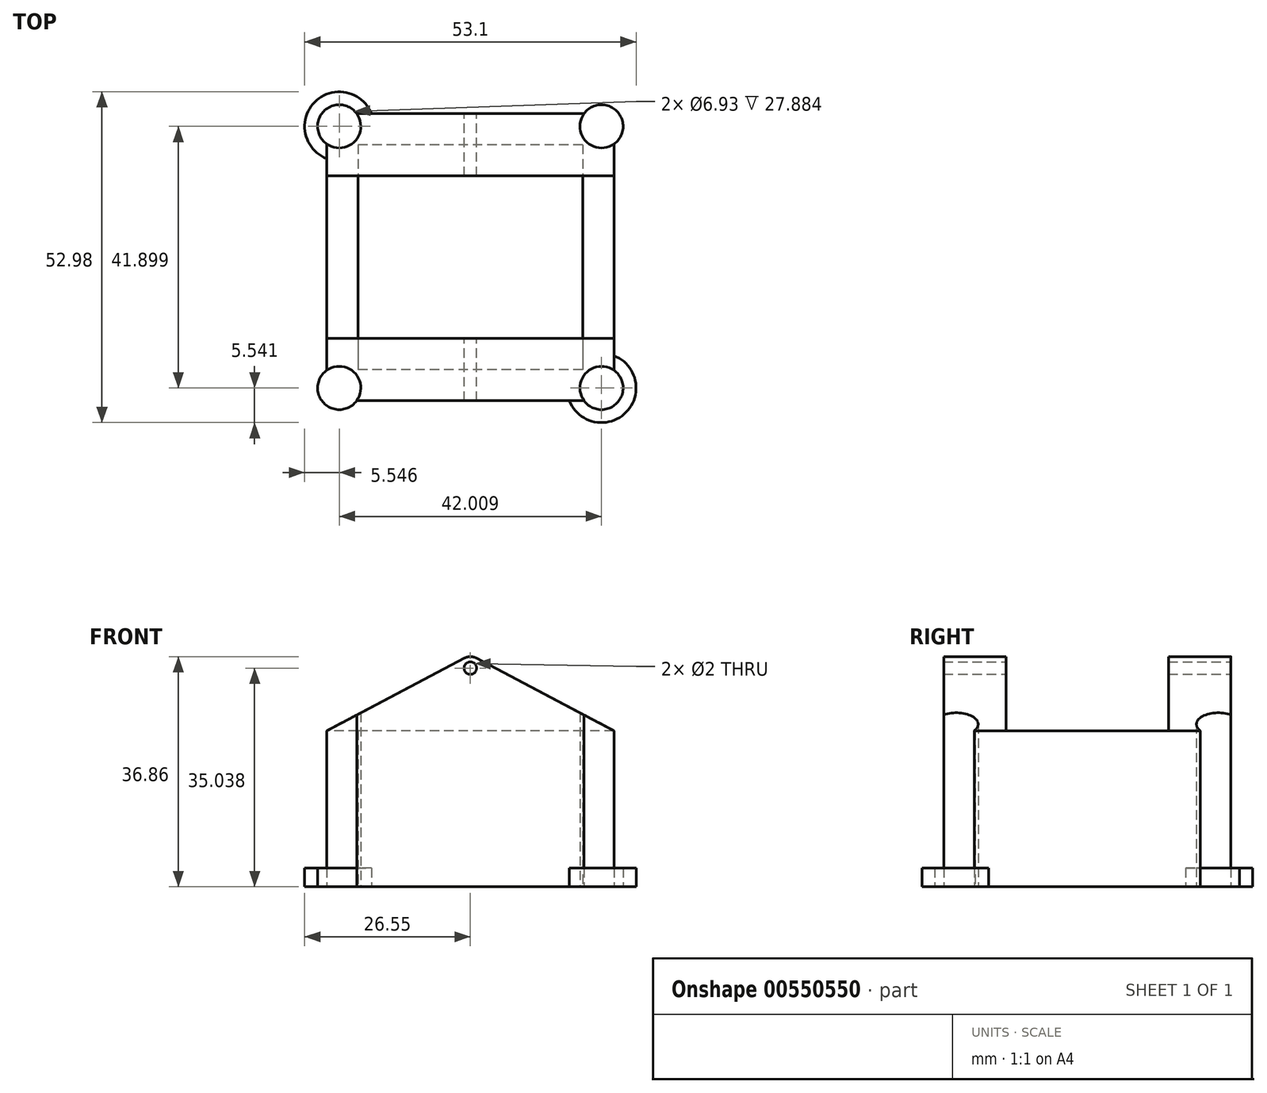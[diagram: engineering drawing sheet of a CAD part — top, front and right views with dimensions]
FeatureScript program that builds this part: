
annotation { "Feature Type Name" : "Feature", "Feature Type Description" : "" }
export const myFeature = defineFeature(function(context is Context, id is Id, definition is map)
    precondition{}
    {
        {
            var Q0;
            Q0=qCreatedBy(makeId("Top.planeOp"),FACE);
            var sketch = newSketch(context, id + "F0", { "sketchPlane" : qUnion([Q0])});
            skLineSegment(sketch, "E0.top", {"start": v(0, 23) * mm, "end": v(-23, 23) * mm});
            skLineSegment(sketch, "E0.right", {"start": v(-23, 0) * mm, "end": v(-23, 23) * mm});
            skCircle(sketch, "E1", {"center": v(-20.22, 20.22) * mm, "radius": 1.65 * mm});
            skCircle(sketch, "E2.MirrorC", {"center": v(20.22, 20.22) * mm, "radius": 1.65 * mm});
            skLineSegment(sketch, "E3.MirrorCS", {"start": v(23, 0) * mm, "end": v(23, 23) * mm});
            skLineSegment(sketch, "E4.MirrorCS", {"start": v(0, 23) * mm, "end": v(23, 23) * mm});
            skLineSegment(sketch, "E5.MirrorCS", {"start": v(0, -23) * mm, "end": v(-23, -23) * mm});
            skCircle(sketch, "E6.MirrorC", {"center": v(-20.22, -20.22) * mm, "radius": 1.65 * mm});
            skLineSegment(sketch, "E7.MirrorCS", {"start": v(-23, 0) * mm, "end": v(-23, -23) * mm});
            skLineSegment(sketch, "E8.MirrorCS", {"start": v(23, 0) * mm, "end": v(23, -23) * mm});
            skCircle(sketch, "E9.MirrorC", {"center": v(20.22, -20.22) * mm, "radius": 1.65 * mm});
            skLineSegment(sketch, "E10.MirrorCS", {"start": v(0, -23) * mm, "end": v(23, -23) * mm});
            skSolve(sketch);
        }
        {
            var Q0;
            Q0 = qSketchRegion(id + "F0", true);
            extrude(context, id + "F1", {"entities" : qUnion([Q0]), "depth" : 25 * mm, "offsetDistance" : 25 * mm});
        }
        {
            var Q0;
            Q0=makeQuery(id+"F1.opExtrude","CAP_FACE",FACE,{"disambiguationData":[OSD([sQuery(id+"F0.wireOp",EDGE,"E0.top"),sQuery(id+"F0.wireOp",EDGE,"E0.right"),sQuery(id+"F0.wireOp",EDGE,"E1"),sQuery(id+"F0.wireOp",EDGE,"E2.MirrorC"),sQuery(id+"F0.wireOp",EDGE,"E3.MirrorCS"),sQuery(id+"F0.wireOp",EDGE,"E4.MirrorCS"),sQuery(id+"F0.wireOp",EDGE,"E5.MirrorCS"),sQuery(id+"F0.wireOp",EDGE,"E6.MirrorC"),sQuery(id+"F0.wireOp",EDGE,"E7.MirrorCS"),sQuery(id+"F0.wireOp",EDGE,"E8.MirrorCS"),sQuery(id+"F0.wireOp",EDGE,"E9.MirrorC"),sQuery(id+"F0.wireOp",EDGE,"E10.MirrorCS")])],"isStart":true});
            var sketch = newSketch(context, id + "F2", { "sketchPlane" : qUnion([Q0])});
            skLineSegment(sketch, "E11.bottom", {"start": v(18, -18) * mm, "end": v(-18, -18) * mm});
            skLineSegment(sketch, "E11.top", {"start": v(18, 18) * mm, "end": v(-18, 18) * mm});
            skLineSegment(sketch, "E11.left", {"start": v(18, -18) * mm, "end": v(18, 18) * mm});
            skLineSegment(sketch, "E11.right", {"start": v(-18, -18) * mm, "end": v(-18, 18) * mm});
            skPoint(sketch, "E11.middle", {"position": v(0, 0) * mm});
            skSolve(sketch);
        }
        {
            var Q0;
            Q0=qCreatedBy(makeId("Front.planeOp"),FACE);
            var sketch = newSketch(context, id + "F3", { "sketchPlane" : qUnion([Q0])});
            skLineSegment(sketch, "E12", {"start": v(0, 25) * mm, "end": v(23, 25) * mm});
            skLineSegment(sketch, "E13", {"start": v(23, 25) * mm, "end": v(0, 37.12) * mm});
            skArc(sketch, "E14", {"start": v(0, 34.04) * mm, "mid": v(1, 35.04) * mm, "end": v(0, 36.04) * mm});
            skArc(sketch, "E15.MirrorCS", {"start": v(0, 34.04) * mm, "mid": v(-1, 35.04) * mm, "end": v(0, 36.04) * mm});
            skLineSegment(sketch, "E16.MirrorCS", {"start": v(-23, 25) * mm, "end": v(0, 37.12) * mm});
            skLineSegment(sketch, "E17.MirrorCS", {"start": v(0, 25) * mm, "end": v(-23, 25) * mm});
            skSolve(sketch);
        }
        {
            var Q0;
            Q0=makeQuery(id+"F3.imprint","IMPRINT",FACE,{"disambiguationData":[TD([[makeQuery(id+"F3.imprint","IMPRINT",EDGE,{"derivedFrom":sQuery(id+"F3.wireOp",EDGE,"E12")}),1.0]])]});
            extrude(context, id + "F4", {"entities" : qUnion([Q0]), "operationType" : NewBodyOperationType.ADD, "endBound" : BoundingType.SYMMETRIC, "depth" : 46 * mm, "offsetDistance" : 25 * mm});
        }
        {
            var Q0;
            Q0=qCreatedBy(makeId("Top.planeOp"),FACE);
            var sketch = newSketch(context, id + "F5", { "sketchPlane" : qUnion([Q0])});
            skCircle(sketch, "E18", {"center": v(-21, 20.95) * mm, "radius": 3.47 * mm});
            skCircle(sketch, "E19.MirrorC", {"center": v(21, 20.95) * mm, "radius": 3.47 * mm});
            skCircle(sketch, "E20.MirrorC", {"center": v(21, -20.95) * mm, "radius": 3.47 * mm});
            skCircle(sketch, "E21.MirrorC", {"center": v(-21, -20.95) * mm, "radius": 3.47 * mm});
            skSolve(sketch);
        }
        {
            var Q0;
            Q0=qCreatedBy(makeId("Top.planeOp"),FACE);
            var sketch = newSketch(context, id + "F6", { "sketchPlane" : qUnion([Q0])});
            skCircle(sketch, "E22", {"center": v(-21, 20.95) * mm, "radius": 5.54 * mm});
            skCircle(sketch, "E23", {"center": v(-21, 20.95) * mm, "radius": 3.47 * mm});
            skCircle(sketch, "E24.MirrorC", {"center": v(21, 20.95) * mm, "radius": 3.47 * mm});
            skCircle(sketch, "E25.MirrorC", {"center": v(21, 20.95) * mm, "radius": 5.54 * mm});
            skCircle(sketch, "E26.MirrorC", {"center": v(-21, -20.95) * mm, "radius": 3.47 * mm});
            skCircle(sketch, "E27.MirrorC", {"center": v(-21, -20.95) * mm, "radius": 5.54 * mm});
            skCircle(sketch, "E28.MirrorC", {"center": v(21, -20.95) * mm, "radius": 3.47 * mm});
            skCircle(sketch, "E29.MirrorC", {"center": v(21, -20.95) * mm, "radius": 5.54 * mm});
            skSolve(sketch);
        }
        {
            var Q0;
            Q0 = qSketchRegion(id + "F3", true);
            extrude(context, id + "F7", {"entities" : qUnion([Q0]), "operationType" : NewBodyOperationType.REMOVE, "endBound" : BoundingType.SYMMETRIC, "oppositeDirection" : true, "depth" : 26 * mm, "offsetDistance" : 25 * mm});
        }
        {
            var Q0;
            Q0 = qSketchRegion(id + "F5", true);
            extrude(context, id + "F8", {"entities" : qUnion([Q0]), "operationType" : NewBodyOperationType.REMOVE, "depth" : 36 * mm, "offsetDistance" : 25 * mm});
        }
        {
            var Q0;
            Q0=makeQuery(id+"F6.imprint","IMPRINT",FACE,{"disambiguationData":[TD([[makeQuery(id+"F6.imprint","IMPRINT",EDGE,{"derivedFrom":sQuery(id+"F6.wireOp",EDGE,"E22")}),1.0]])]});
            var Q1;
            Q1=makeQuery(id+"F6.imprint","IMPRINT",FACE,{"disambiguationData":[TD([[makeQuery(id+"F6.imprint","IMPRINT",EDGE,{"derivedFrom":sQuery(id+"F6.wireOp",EDGE,"E24.MirrorC")}),1.0]])]});
            var Q2;
            Q2=makeQuery(id+"F6.imprint","IMPRINT",FACE,{"disambiguationData":[TD([[makeQuery(id+"F6.imprint","IMPRINT",EDGE,{"derivedFrom":sQuery(id+"F6.wireOp",EDGE,"E28.MirrorC")}),-1.0]])]});
            var Q3;
            Q3=makeQuery(id+"F6.imprint","IMPRINT",FACE,{"disambiguationData":[TD([[makeQuery(id+"F6.imprint","IMPRINT",EDGE,{"derivedFrom":sQuery(id+"F6.wireOp",EDGE,"E26.MirrorC")}),1.0]])]});
            extrude(context, id + "F9", {"entities" : qUnion([Q0, Q1, Q2, Q3]), "operationType" : NewBodyOperationType.ADD, "depth" : 3 * mm, "offsetDistance" : 25 * mm});
        }
        {
            var Q0;
            Q0 = qSketchRegion(id + "F2", true);
            extrude(context, id + "F10", {"entities" : qUnion([Q0]), "operationType" : NewBodyOperationType.REMOVE, "oppositeDirection" : true, "depth" : 25 * mm, "offsetDistance" : 25 * mm});
        }
        {
            var Q0;
            {var subQ0=sQuery(id+"F3.wireOp",EDGE,"E13");var subQ2=sQuery(id+"F3.wireOp",EDGE,"E16.MirrorCS");Q0=makeQuery(id+"F7.boolean.opBoolean","SPLIT",EDGE,{"disambiguationData":[TD([makeQuery(id+"F1.opExtrude","SWEPT_FACE",FACE,{"disambiguationData":[OSD([sQuery(id+"F0.wireOp",EDGE,"E0.top"),sQuery(id+"F0.wireOp",EDGE,"E4.MirrorCS")])]})])],"derivedFrom":makeQuery(id+"F4.opExtrude","SWEPT_EDGE",EDGE,{"disambiguationData":[OSD([subQ0,subQ2])]})});}
            var Q1;
            {var subQ0=sQuery(id+"F3.wireOp",EDGE,"E16.MirrorCS");var subQ1=sQuery(id+"F3.wireOp",EDGE,"E13");Q1=makeQuery(id+"F7.boolean.opBoolean","SPLIT",EDGE,{"disambiguationData":[TD([makeQuery(id+"F1.opExtrude","SWEPT_FACE",FACE,{"disambiguationData":[OSD([sQuery(id+"F0.wireOp",EDGE,"E5.MirrorCS"),sQuery(id+"F0.wireOp",EDGE,"E10.MirrorCS")])]})])],"derivedFrom":makeQuery(id+"F4.opExtrude","SWEPT_EDGE",EDGE,{"disambiguationData":[OSD([subQ1,subQ0])]})});}
            fillet(context, id + "F11", {"entities" : qUnion([Q0, Q1]), "radius" : 2 * mm, "tangentPropagation" : true, "allowEdgeOverflow" : false});
        }
    });
